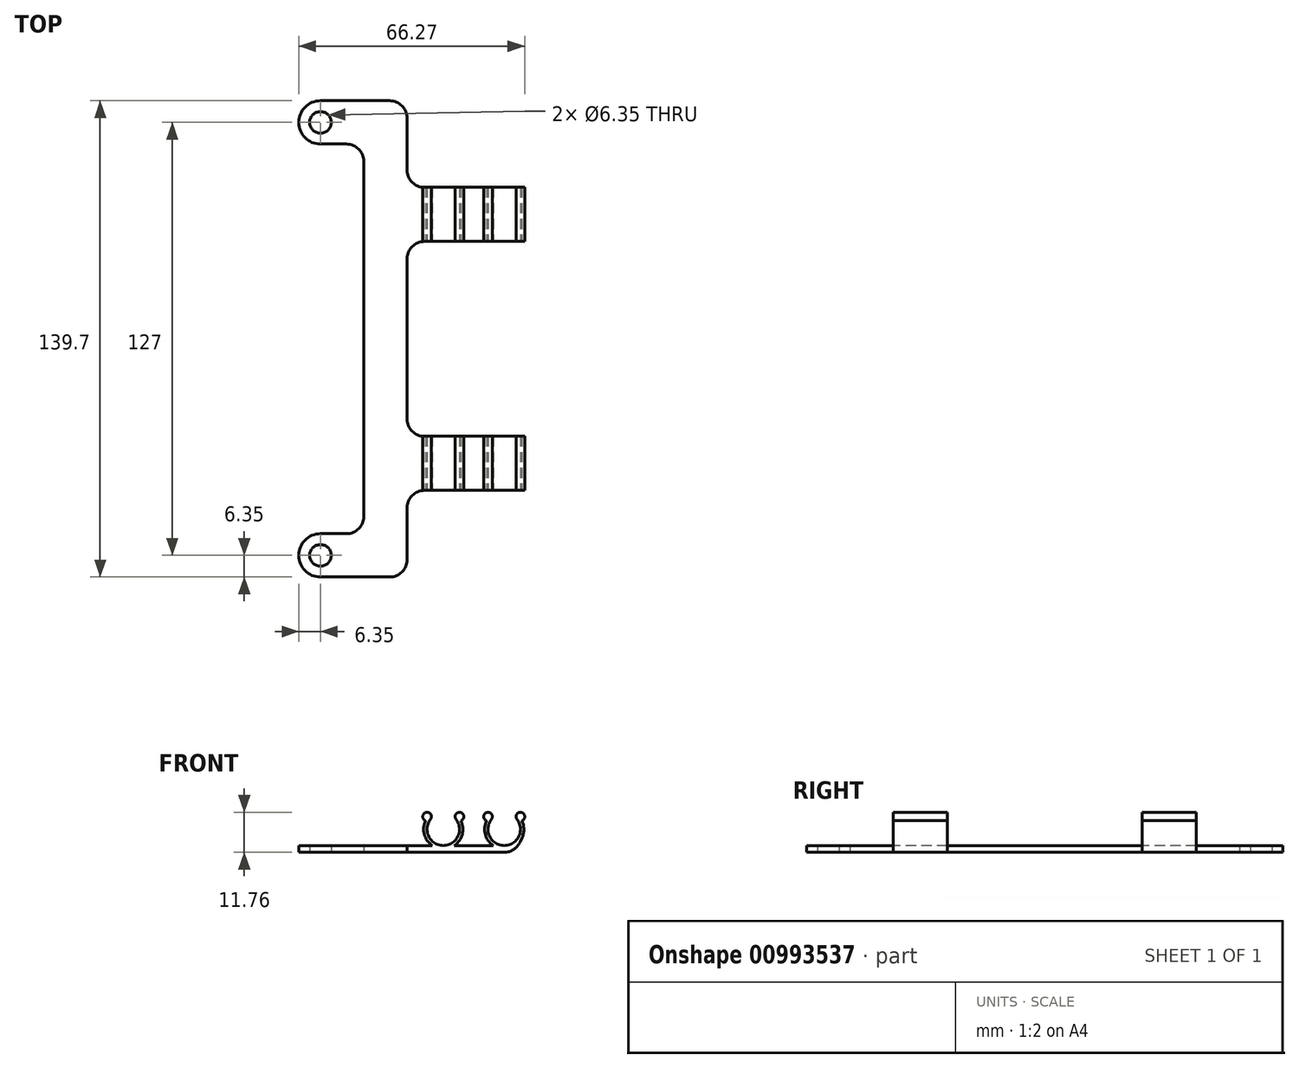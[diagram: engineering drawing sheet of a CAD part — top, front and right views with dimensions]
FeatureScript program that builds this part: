
annotation { "Feature Type Name" : "Feature", "Feature Type Description" : "" }
export const myFeature = defineFeature(function(context is Context, id is Id, definition is map)
    precondition{}
    {
        {
            var Q0;
            Q0=qCreatedBy(makeId("Top.planeOp"),FACE);
            var sketch = newSketch(context, id + "F0", { "sketchPlane" : qUnion([Q0])});
            skLineSegment(sketch, "E0", {"start": v(6.35, 0) * mm, "end": v(31.75, 0) * mm});
            skLineSegment(sketch, "E1", {"start": v(31.75, 0) * mm, "end": v(31.75, 25.4) * mm});
            skLineSegment(sketch, "E2", {"start": v(31.75, 25.4) * mm, "end": v(63.5, 25.4) * mm});
            skLineSegment(sketch, "E3", {"start": v(63.5, 25.4) * mm, "end": v(63.5, 41.28) * mm});
            skLineSegment(sketch, "E4", {"start": v(63.5, 41.28) * mm, "end": v(31.75, 41.28) * mm});
            skLineSegment(sketch, "E5", {"start": v(31.75, 41.28) * mm, "end": v(31.75, 98.42) * mm});
            skLineSegment(sketch, "E6", {"start": v(31.75, 98.42) * mm, "end": v(63.5, 98.42) * mm});
            skLineSegment(sketch, "E7", {"start": v(63.5, 98.42) * mm, "end": v(63.5, 114.3) * mm});
            skLineSegment(sketch, "E8", {"start": v(31.75, 114.3) * mm, "end": v(31.75, 139.7) * mm});
            skLineSegment(sketch, "E9", {"start": v(31.75, 139.7) * mm, "end": v(6.35, 139.7) * mm});
            skLineSegment(sketch, "E10", {"start": v(6.35, 127) * mm, "end": v(19.05, 127) * mm});
            skLineSegment(sketch, "E11", {"start": v(19.05, 127) * mm, "end": v(19.05, 12.7) * mm});
            skLineSegment(sketch, "E12", {"start": v(19.05, 12.7) * mm, "end": v(6.35, 12.7) * mm});
            skLineSegment(sketch, "E13", {"start": v(31.75, 69.85) * mm, "end": v(19.05, 69.85) * mm, "construction": true});
            skLineSegment(sketch, "E14", {"start": v(0, 133.35) * mm, "end": v(31.75, 133.35) * mm, "construction": true});
            skLineSegment(sketch, "E15", {"start": v(0, 6.35) * mm, "end": v(31.75, 6.35) * mm, "construction": true});
            skCircle(sketch, "E16", {"center": v(6.35, 133.35) * mm, "radius": 3.18 * mm});
            skArc(sketch, "E17", {"start": v(6.35, 139.7) * mm, "mid": v(0, 133.35) * mm, "end": v(6.35, 127) * mm});
            skPoint(sketch, "E18.orphan", {"position": v(0, 139.7) * mm});
            skPoint(sketch, "E19.orphan", {"position": v(0, 127) * mm});
            skArc(sketch, "E20", {"start": v(6.35, 12.7) * mm, "mid": v(0, 6.35) * mm, "end": v(6.35, 0) * mm});
            skCircle(sketch, "E21", {"center": v(6.35, 6.35) * mm, "radius": 3.18 * mm});
            skPoint(sketch, "E22.orphan", {"position": v(0, 12.7) * mm});
            skPoint(sketch, "E23.end.orphan", {"position": v(0, 0) * mm});
            skLineSegment(sketch, "E24", {"start": v(31.75, 114.3) * mm, "end": v(63.5, 114.3) * mm});
            skSolve(sketch);
        }
        {
            var Q0;
            Q0 = qSketchRegion(id + "F0", true);
            extrude(context, id + "F1", {"entities" : qUnion([Q0]), "depth" : 2 * mm, "offsetDistance" : 25.4 * mm});
        }
        {
            var Q0;
            Q0=makeQuery(id+"F1.opExtrude","SWEPT_FACE",FACE,{"disambiguationData":[OSD([sQuery(id+"F0.wireOp",EDGE,"E2")])]});
            var sketch = newSketch(context, id + "F2", { "sketchPlane" : qUnion([Q0])});
            skArc(sketch, "E25", {"start": v(55.08, 9.3) * mm, "mid": v(60.26, 1) * mm, "end": v(65.43, 9.3) * mm});
            skArc(sketch, "E26", {"start": v(56.5, 9.7) * mm, "mid": v(60.26, 2) * mm, "end": v(64, 9.7) * mm});
            skLineSegment(sketch, "E27", {"start": v(60.26, 6.76) * mm, "end": v(60.26, 20.65) * mm, "construction": true});
            skLineSegment(sketch, "E28.0", {"start": v(64, 9.7) * mm, "end": v(64, 11.14) * mm, "construction": true});
            skLineSegment(sketch, "E29.0", {"start": v(56.5, 9.7) * mm, "end": v(56.5, 11.14) * mm, "construction": true});
            skArc(sketch, "E30", {"start": v(56.5, 9.7) * mm, "mid": v(55.16, 11.7) * mm, "end": v(55.08, 9.3) * mm});
            skArc(sketch, "E31.MirrorC", {"start": v(64, 9.7) * mm, "mid": v(65.35, 11.7) * mm, "end": v(65.43, 9.3) * mm});
            skLineSegment(sketch, "E32", {"start": v(51.32, 2) * mm, "end": v(51.32, 33.75) * mm, "construction": true});
            skArc(sketch, "E33.MirrorCS", {"start": v(38.63, 9.7) * mm, "mid": v(37.29, 11.7) * mm, "end": v(37.2, 9.3) * mm});
            skArc(sketch, "E34.MirrorCS", {"start": v(47.56, 9.3) * mm, "mid": v(42.38, 1) * mm, "end": v(37.2, 9.3) * mm});
            skArc(sketch, "E35.MirrorCS", {"start": v(46.13, 9.7) * mm, "mid": v(47.48, 11.7) * mm, "end": v(47.56, 9.3) * mm});
            skArc(sketch, "E36.MirrorCS", {"start": v(46.13, 9.7) * mm, "mid": v(42.38, 2) * mm, "end": v(38.63, 9.7) * mm});
            skPoint(sketch, "E37", {"position": v(51.32, 2) * mm});
            skSolve(sketch);
        }
        {
            var Q0;
            Q0 = qSketchRegion(id + "F2", true);
            var Q1;
            Q1=makeQuery(id+"F1.opExtrude","SWEPT_FACE",FACE,{"disambiguationData":[OSD([sQuery(id+"F0.wireOp",EDGE,"E24")])]});
            extrude(context, id + "F3", {"entities" : qUnion([Q0]), "operationType" : NewBodyOperationType.ADD, "endBound" : BoundingType.UP_TO_SURFACE, "oppositeDirection" : true, "depth" : 25.4 * mm, "endBoundEntityFace" : qUnion([Q1]), "offsetDistance" : 25.4 * mm});
        }
        {
            var Q0;
            Q0=makeQuery(id+"F3.boolean.opBoolean","MERGE",FACE,{"derivedFrom":[makeQuery(id+"F1.opExtrude","SWEPT_FACE",FACE,{"disambiguationData":[OSD([sQuery(id+"F0.wireOp",EDGE,"E2")])]}),makeQuery(id+"F3.opExtrude","CAP_FACE",FACE,{"disambiguationData":[OSD([sQuery(id+"F2.wireOp",EDGE,"E25"),sQuery(id+"F2.wireOp",EDGE,"E26"),sQuery(id+"F2.wireOp",EDGE,"E30"),sQuery(id+"F2.wireOp",EDGE,"E31.MirrorC")])],"isStart":true}),makeQuery(id+"F3.opExtrude","CAP_FACE",FACE,{"disambiguationData":[OSD([sQuery(id+"F2.wireOp",EDGE,"E33.MirrorCS"),sQuery(id+"F2.wireOp",EDGE,"E34.MirrorCS"),sQuery(id+"F2.wireOp",EDGE,"E35.MirrorCS"),sQuery(id+"F2.wireOp",EDGE,"E36.MirrorCS")])],"isStart":true})]});
            var sketch = newSketch(context, id + "F4", { "sketchPlane" : qUnion([Q0])});
            skLineSegment(sketch, "E38", {"start": v(65.5, 4.37) * mm, "end": v(63.5, 0) * mm});
            skLineSegment(sketch, "E39", {"start": v(65.5, 4.37) * mm, "end": v(63.5, 2) * mm});
            skLineSegment(sketch, "E40", {"start": v(63.5, 2) * mm, "end": v(63.5, 0) * mm});
            skSolve(sketch);
        }
        {
            var Q0;
            Q0 = qSketchRegion(id + "F4", true);
            var Q1;
            Q1=makeQuery(id+"F3.boolean.opBoolean","MERGE",FACE,{"derivedFrom":[makeQuery(id+"F1.opExtrude","SWEPT_FACE",FACE,{"disambiguationData":[OSD([sQuery(id+"F0.wireOp",EDGE,"E24")])]}),makeQuery(id+"F3.opExtrude","CAP_FACE",FACE,{"disambiguationData":[OSD([sQuery(id+"F2.wireOp",EDGE,"E25"),sQuery(id+"F2.wireOp",EDGE,"E26"),sQuery(id+"F2.wireOp",EDGE,"E30"),sQuery(id+"F2.wireOp",EDGE,"E31.MirrorC")])],"isStart":false}),makeQuery(id+"F3.opExtrude","CAP_FACE",FACE,{"disambiguationData":[OSD([sQuery(id+"F2.wireOp",EDGE,"E33.MirrorCS"),sQuery(id+"F2.wireOp",EDGE,"E34.MirrorCS"),sQuery(id+"F2.wireOp",EDGE,"E35.MirrorCS"),sQuery(id+"F2.wireOp",EDGE,"E36.MirrorCS")])],"isStart":false})]});
            extrude(context, id + "F5", {"entities" : qUnion([Q0]), "operationType" : NewBodyOperationType.ADD, "endBound" : BoundingType.UP_TO_SURFACE, "oppositeDirection" : true, "depth" : 25.4 * mm, "endBoundEntityFace" : qUnion([Q1]), "offsetDistance" : 25.4 * mm});
        }
        {
            var Q0;
            Q0=makeQuery(id+"F1.opExtrude","CAP_FACE",FACE,{"disambiguationData":[OSD([sQuery(id+"F0.wireOp",EDGE,"E0"),sQuery(id+"F0.wireOp",EDGE,"E1"),sQuery(id+"F0.wireOp",EDGE,"E2"),sQuery(id+"F0.wireOp",EDGE,"E3"),sQuery(id+"F0.wireOp",EDGE,"E4"),sQuery(id+"F0.wireOp",EDGE,"E5"),sQuery(id+"F0.wireOp",EDGE,"E6"),sQuery(id+"F0.wireOp",EDGE,"E7"),sQuery(id+"F0.wireOp",EDGE,"E8"),sQuery(id+"F0.wireOp",EDGE,"E9"),sQuery(id+"F0.wireOp",EDGE,"E10"),sQuery(id+"F0.wireOp",EDGE,"E11"),sQuery(id+"F0.wireOp",EDGE,"E12"),sQuery(id+"F0.wireOp",EDGE,"E16"),sQuery(id+"F0.wireOp",EDGE,"E17"),sQuery(id+"F0.wireOp",EDGE,"E20"),sQuery(id+"F0.wireOp",EDGE,"E21"),sQuery(id+"F0.wireOp",EDGE,"E24")])],"isStart":true});
            var sketch = newSketch(context, id + "F6", { "sketchPlane" : qUnion([Q0])});
            skLineSegment(sketch, "E41.bottom", {"start": v(31.75, -41.28) * mm, "end": v(76.2, -41.28) * mm});
            skLineSegment(sketch, "E41.top", {"start": v(31.75, -98.42) * mm, "end": v(76.2, -98.42) * mm});
            skLineSegment(sketch, "E41.left", {"start": v(31.75, -41.28) * mm, "end": v(31.75, -98.42) * mm});
            skLineSegment(sketch, "E41.right", {"start": v(76.2, -41.28) * mm, "end": v(76.2, -98.42) * mm});
            skSolve(sketch);
        }
        {
            var Q0;
            Q0 = qSketchRegion(id + "F6", true);
            extrude(context, id + "F7", {"entities" : qUnion([Q0]), "operationType" : NewBodyOperationType.REMOVE, "oppositeDirection" : true, "depth" : 25.4 * mm, "offsetDistance" : 25.4 * mm});
        }
        {
            var Q0;
            {var subQ0=sQuery(id+"F0.wireOp",EDGE,"E11");var subQ1=sQuery(id+"F2.wireOp",EDGE,"E34.MirrorCS");var subQ2=sQuery(id+"F0.wireOp",EDGE,"E10");var subQ3=sQuery(id+"F2.wireOp",EDGE,"E36.MirrorCS");var subQ4=sQuery(id+"F2.wireOp",EDGE,"E35.MirrorCS");var subQ5=sQuery(id+"F2.wireOp",EDGE,"E33.MirrorCS");var subQ6=sQuery(id+"F0.wireOp",EDGE,"E8");var subQ7=sQuery(id+"F0.wireOp",EDGE,"E6");var subQ8=sQuery(id+"F0.wireOp",EDGE,"E5");var subQ9=sQuery(id+"F0.wireOp",EDGE,"E9");var subQ10=sQuery(id+"F0.wireOp",EDGE,"E0");var subQ11=sQuery(id+"F0.wireOp",EDGE,"E1");var subQ12=sQuery(id+"F0.wireOp",EDGE,"E2");var subQ13=sQuery(id+"F0.wireOp",EDGE,"E4");var subQ14=sQuery(id+"F2.wireOp",EDGE,"E31.MirrorC");var subQ15=sQuery(id+"F2.wireOp",EDGE,"E30");var subQ16=sQuery(id+"F2.wireOp",EDGE,"E26");var subQ17=sQuery(id+"F2.wireOp",EDGE,"E25");var subQ18=sQuery(id+"F0.wireOp",EDGE,"E12");var subQ19=sQuery(id+"F0.wireOp",EDGE,"E16");var subQ20=sQuery(id+"F0.wireOp",EDGE,"E17");var subQ21=sQuery(id+"F0.wireOp",EDGE,"E20");var subQ22=sQuery(id+"F0.wireOp",EDGE,"E21");var subQ23=sQuery(id+"F0.wireOp",EDGE,"E24");Q0=makeQuery(id+"F3.boolean.opBoolean","SPLIT",FACE,{"disambiguationData":[TD([makeQuery(id+"F1.opExtrude","SWEPT_FACE",FACE,{"disambiguationData":[OSD([subQ10])]}),makeQuery(id+"F1.opExtrude","SWEPT_FACE",FACE,{"disambiguationData":[OSD([subQ11])]}),makeQuery(id+"F1.opExtrude","SWEPT_FACE",FACE,{"disambiguationData":[OSD([subQ12])]}),makeQuery(id+"F1.opExtrude","SWEPT_FACE",FACE,{"disambiguationData":[OSD([subQ13])]}),makeQuery(id+"F1.opExtrude","SWEPT_FACE",FACE,{"disambiguationData":[OSD([subQ8])]}),makeQuery(id+"F1.opExtrude","SWEPT_FACE",FACE,{"disambiguationData":[OSD([subQ7])]}),makeQuery(id+"F1.opExtrude","SWEPT_FACE",FACE,{"disambiguationData":[OSD([subQ6])]}),makeQuery(id+"F1.opExtrude","SWEPT_FACE",FACE,{"disambiguationData":[OSD([subQ9])]}),makeQuery(id+"F1.opExtrude","SWEPT_FACE",FACE,{"disambiguationData":[OSD([subQ2])]}),makeQuery(id+"F1.opExtrude","SWEPT_FACE",FACE,{"disambiguationData":[OSD([subQ0])]}),makeQuery(id+"F1.opExtrude","SWEPT_FACE",FACE,{"disambiguationData":[OSD([subQ18])]}),makeQuery(id+"F1.opExtrude","SWEPT_FACE",FACE,{"disambiguationData":[OSD([subQ19])]}),makeQuery(id+"F1.opExtrude","SWEPT_FACE",FACE,{"disambiguationData":[OSD([subQ20])]}),makeQuery(id+"F1.opExtrude","SWEPT_FACE",FACE,{"disambiguationData":[OSD([subQ21])]}),makeQuery(id+"F1.opExtrude","SWEPT_FACE",FACE,{"disambiguationData":[OSD([subQ22])]}),makeQuery(id+"F1.opExtrude","SWEPT_FACE",FACE,{"disambiguationData":[OSD([subQ23])]}),makeQuery(id+"F3.opExtrude","CAP_FACE",FACE,{"disambiguationData":[OSD([subQ17,subQ16,subQ15,subQ14])],"isStart":true}),makeQuery(id+"F3.opExtrude","CAP_FACE",FACE,{"disambiguationData":[OSD([subQ17,subQ16,subQ15,subQ14])],"isStart":false}),makeQuery(id+"F3.opExtrude","CAP_FACE",FACE,{"disambiguationData":[OSD([subQ5,subQ1,subQ4,subQ3])],"isStart":true}),makeQuery(id+"F3.opExtrude","CAP_FACE",FACE,{"disambiguationData":[OSD([subQ5,subQ1,subQ4,subQ3])],"isStart":false}),makeQuery(id+"F3.opExtrude","SWEPT_FACE",FACE,{"disambiguationData":[OSD([subQ1])]})])],"derivedFrom":makeQuery(id+"F1.opExtrude","CAP_FACE",FACE,{"disambiguationData":[OSD([subQ10,subQ11,subQ12,sQuery(id+"F0.wireOp",EDGE,"E3"),subQ13,subQ8,subQ7,sQuery(id+"F0.wireOp",EDGE,"E7"),subQ6,subQ9,subQ2,subQ0,subQ18,subQ19,subQ20,subQ21,subQ22,subQ23])],"isStart":false})});}
            var sketch = newSketch(context, id + "F8", { "sketchPlane" : qUnion([Q0])});
            skLineSegment(sketch, "E42.bottom", {"start": v(63.5, 41.28) * mm, "end": v(19.05, 41.28) * mm});
            skLineSegment(sketch, "E42.top", {"start": v(63.5, 98.42) * mm, "end": v(19.05, 98.42) * mm});
            skLineSegment(sketch, "E42.left", {"start": v(63.5, 41.28) * mm, "end": v(63.5, 98.42) * mm});
            skLineSegment(sketch, "E42.right", {"start": v(19.05, 41.28) * mm, "end": v(19.05, 98.42) * mm});
            skPoint(sketch, "E42.middle", {"position": v(41.28, 69.85) * mm});
            skSolve(sketch);
        }
        {
            var Q0;
            Q0 = qSketchRegion(id + "F8", true);
            extrude(context, id + "F9", {"entities" : qUnion([Q0]), "operationType" : NewBodyOperationType.REMOVE, "depth" : 25.4 * mm, "offsetDistance" : 25.4 * mm});
        }
        {
            var Q0;
            Q0=makeQuery(id+"F3.boolean.opBoolean","MERGE",FACE,{"derivedFrom":[makeQuery(id+"F1.opExtrude","SWEPT_FACE",FACE,{"disambiguationData":[OSD([sQuery(id+"F0.wireOp",EDGE,"E2")])]}),makeQuery(id+"F3.opExtrude","CAP_FACE",FACE,{"disambiguationData":[OSD([sQuery(id+"F2.wireOp",EDGE,"E25"),sQuery(id+"F2.wireOp",EDGE,"E26"),sQuery(id+"F2.wireOp",EDGE,"E30"),sQuery(id+"F2.wireOp",EDGE,"E31.MirrorC")])],"isStart":true}),makeQuery(id+"F3.opExtrude","CAP_FACE",FACE,{"disambiguationData":[OSD([sQuery(id+"F2.wireOp",EDGE,"E33.MirrorCS"),sQuery(id+"F2.wireOp",EDGE,"E34.MirrorCS"),sQuery(id+"F2.wireOp",EDGE,"E35.MirrorCS"),sQuery(id+"F2.wireOp",EDGE,"E36.MirrorCS")])],"isStart":true})]});
            var sketch = newSketch(context, id + "F10", { "sketchPlane" : qUnion([Q0])});
            skCircle(sketch, "E43", {"center": v(42.38, 6.76) * mm, "radius": 4.76 * mm});
            skCircle(sketch, "E44", {"center": v(60.26, 6.76) * mm, "radius": 4.76 * mm});
            skSolve(sketch);
        }
        {
            var Q0;
            Q0 = qSketchRegion(id + "F10", true);
            var Q1;
            Q1=makeQuery(id+"F3.boolean.opBoolean","MERGE",FACE,{"derivedFrom":[makeQuery(id+"F1.opExtrude","SWEPT_FACE",FACE,{"disambiguationData":[OSD([sQuery(id+"F0.wireOp",EDGE,"E24")])]}),makeQuery(id+"F3.opExtrude","CAP_FACE",FACE,{"disambiguationData":[OSD([sQuery(id+"F2.wireOp",EDGE,"E25"),sQuery(id+"F2.wireOp",EDGE,"E26"),sQuery(id+"F2.wireOp",EDGE,"E30"),sQuery(id+"F2.wireOp",EDGE,"E31.MirrorC")])],"isStart":false}),makeQuery(id+"F3.opExtrude","CAP_FACE",FACE,{"disambiguationData":[OSD([sQuery(id+"F2.wireOp",EDGE,"E33.MirrorCS"),sQuery(id+"F2.wireOp",EDGE,"E34.MirrorCS"),sQuery(id+"F2.wireOp",EDGE,"E35.MirrorCS"),sQuery(id+"F2.wireOp",EDGE,"E36.MirrorCS")])],"isStart":false})]});
            extrude(context, id + "F11", {"entities" : qUnion([Q0]), "operationType" : NewBodyOperationType.REMOVE, "endBound" : BoundingType.UP_TO_SURFACE, "oppositeDirection" : true, "depth" : 25.4 * mm, "endBoundEntityFace" : qUnion([Q1]), "offsetDistance" : 25.4 * mm});
        }
        {
            var Q0;
            Q0=makeQuery(id+"F1.opExtrude","SWEPT_EDGE",EDGE,{"disambiguationData":[OSD([sQuery(id+"F0.wireOp",EDGE,"E0"),sQuery(id+"F0.wireOp",EDGE,"E1")])]});
            var Q1;
            Q1=makeQuery(id+"F1.opExtrude","SWEPT_EDGE",EDGE,{"disambiguationData":[OSD([sQuery(id+"F0.wireOp",EDGE,"E1"),sQuery(id+"F0.wireOp",EDGE,"E2")])]});
            var Q2;
            Q2=makeQuery(id+"F1.opExtrude","SWEPT_EDGE",EDGE,{"disambiguationData":[OSD([sQuery(id+"F0.wireOp",EDGE,"E4"),sQuery(id+"F0.wireOp",EDGE,"E5")])]});
            var Q3;
            Q3=makeQuery(id+"F1.opExtrude","SWEPT_EDGE",EDGE,{"disambiguationData":[OSD([sQuery(id+"F0.wireOp",EDGE,"E5"),sQuery(id+"F0.wireOp",EDGE,"E6")])]});
            var Q4;
            Q4=makeQuery(id+"F1.opExtrude","SWEPT_EDGE",EDGE,{"disambiguationData":[OSD([sQuery(id+"F0.wireOp",EDGE,"E8"),sQuery(id+"F0.wireOp",EDGE,"E24")])]});
            var Q5;
            Q5=makeQuery(id+"F1.opExtrude","SWEPT_EDGE",EDGE,{"disambiguationData":[OSD([sQuery(id+"F0.wireOp",EDGE,"E8"),sQuery(id+"F0.wireOp",EDGE,"E9")])]});
            var Q6;
            Q6=makeQuery(id+"F1.opExtrude","SWEPT_EDGE",EDGE,{"disambiguationData":[OSD([sQuery(id+"F0.wireOp",EDGE,"E10"),sQuery(id+"F0.wireOp",EDGE,"E11")])]});
            var Q7;
            Q7=makeQuery(id+"F1.opExtrude","SWEPT_EDGE",EDGE,{"disambiguationData":[OSD([sQuery(id+"F0.wireOp",EDGE,"E11"),sQuery(id+"F0.wireOp",EDGE,"E12")])]});
            fillet(context, id + "F12", {"entities" : qUnion([Q0, Q1, Q2, Q3, Q4, Q5, Q6, Q7]), "radius" : 5.08 * mm, "tangentPropagation" : true, "allowEdgeOverflow" : false});
        }
        {
            var Q0;
            Q0=makeQuery(id+"F5.boolean.opBoolean","MERGE",EDGE,{"derivedFrom":[makeQuery(id+"F1.opExtrude","CAP_EDGE",EDGE,{"disambiguationData":[OSD([sQuery(id+"F0.wireOp",EDGE,"E3")])],"isStart":true}),makeQuery(id+"F5.opExtrude","SWEPT_EDGE",EDGE,{"disambiguationData":[OSD([sQuery(id+"F0.wireOp",EDGE,"E2"),sQuery(id+"F4.wireOp",EDGE,"E38"),sQuery(id+"F4.wireOp",EDGE,"E40")])]})]});
            var Q1;
            Q1=makeQuery(id+"F5.boolean.opBoolean","MERGE",EDGE,{"derivedFrom":[makeQuery(id+"F1.opExtrude","CAP_EDGE",EDGE,{"disambiguationData":[OSD([sQuery(id+"F0.wireOp",EDGE,"E7")])],"isStart":true}),makeQuery(id+"F5.opExtrude","SWEPT_EDGE",EDGE,{"disambiguationData":[OSD([sQuery(id+"F0.wireOp",EDGE,"E2"),sQuery(id+"F4.wireOp",EDGE,"E38"),sQuery(id+"F4.wireOp",EDGE,"E40")])]})]});
            fillet(context, id + "F13", {"entities" : qUnion([Q0, Q1]), "radius" : 5.08 * mm, "tangentPropagation" : true, "allowEdgeOverflow" : false});
        }
    });
